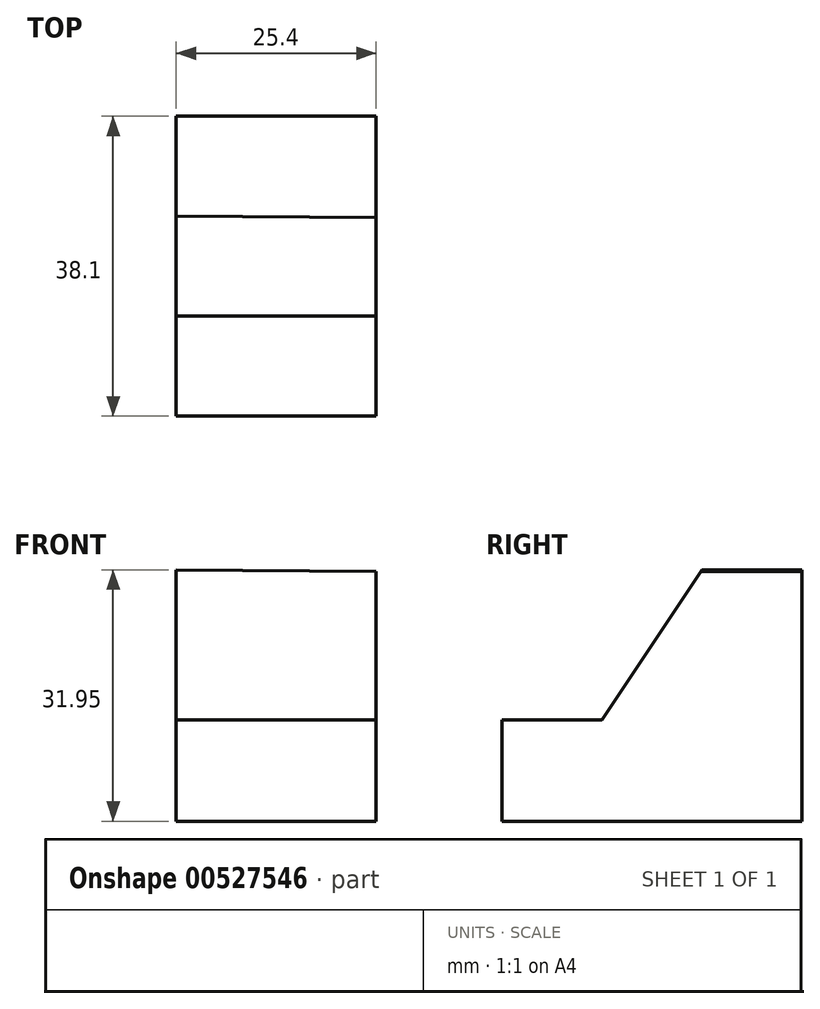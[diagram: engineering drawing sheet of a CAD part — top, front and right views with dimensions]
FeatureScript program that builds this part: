
annotation { "Feature Type Name" : "Feature", "Feature Type Description" : "" }
export const myFeature = defineFeature(function(context is Context, id is Id, definition is map)
    precondition{}
    {
        {
            var Q0;
            Q0=qCreatedBy(makeId("Front.planeOp"),FACE);
            var sketch = newSketch(context, id + "F0", { "sketchPlane" : qUnion([Q0])});
            skLineSegment(sketch, "E0", {"start": v(0, 0) * mm, "end": v(0, 31.95) * mm});
            skLineSegment(sketch, "E1", {"start": v(0, 0) * mm, "end": v(25.4, 0) * mm});
            skLineSegment(sketch, "E2", {"start": v(25.4, 0) * mm, "end": v(25.4, 31.75) * mm});
            skLineSegment(sketch, "E3", {"start": v(25.4, 31.75) * mm, "end": v(0, 31.95) * mm});
            skSolve(sketch);
        }
        {
            var Q0;
            Q0=makeQuery(id+"F0.imprint","IMPRINT",FACE,{"disambiguationData":[TD([[makeQuery(id+"F0.imprint","IMPRINT",EDGE,{"derivedFrom":sQuery(id+"F0.wireOp",EDGE,"E0")}),-1.0]])]});
            extrude(context, id + "F1", {"entities" : qUnion([Q0]), "depth" : 38.1 * mm, "offsetDistance" : 25.4 * mm});
        }
        {
            var Q0;
            Q0=makeQuery(id+"F1.opExtrude","SWEPT_FACE",FACE,{"disambiguationData":[OSD([sQuery(id+"F0.wireOp",EDGE,"E0")])]});
            var sketch = newSketch(context, id + "F2", { "sketchPlane" : qUnion([Q0])});
            skPoint(sketch, "E4.end.orphan", {"position": v(21.98, 12.9) * mm});
            skLineSegment(sketch, "E5", {"start": v(12.7, 31.95) * mm, "end": v(25.4, 12.9) * mm});
            skPoint(sketch, "E6.orphan", {"position": v(38.1, 12.9) * mm});
            skLineSegment(sketch, "E7", {"start": v(38.1, 12.9) * mm, "end": v(25.4, 12.9) * mm});
            skPoint(sketch, "E8.start.orphan", {"position": v(12.7, 12.9) * mm});
            skSolve(sketch);
        }
        {
            var Q0;
            {var subQ0=sQuery(id+"F2.wireOp",EDGE,"E5");Q0=makeQuery(id+"F2.imprint","IMPRINT",FACE,{"disambiguationData":[TD([[makeQuery(id+"F2.imprint","IMPRINT",EDGE,{"derivedFrom":subQ0}),1.0]])]});}
            extrude(context, id + "F3", {"entities" : qUnion([Q0]), "operationType" : NewBodyOperationType.REMOVE, "oppositeDirection" : true, "depth" : 25.4 * mm, "offsetDistance" : 25.4 * mm});
        }
    });
